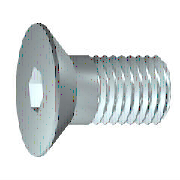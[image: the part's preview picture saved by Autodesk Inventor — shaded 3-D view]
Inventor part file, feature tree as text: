
AUTODESK INVENTOR PART (.ipt)
format: ipt  version: 2020 (Build 240168000, 168)  size: 186,368 bytes
history: native  units: mm (DEFAULTED — no unit token found)
features: other x4, sketch x3, fillet x1, chamfer x1
ambient origin geometry x8: Origin, YZ Plane, XZ Plane, XY Plane, X Axis, Y Axis, Z Axis, Center Point
bodies: Solid1 (feature_tree)
feature tree (9):
  sketch  "Sketch1"  dims[d2=3.0mm]
  other  "WorkPoint1"
  sketch  "Sketch2"  dims[d3=3.0mm]
  fillet  "Fillet1"  [1 undecoded]
  chamfer  "Chamfer1"  Distance=1.5mm
  other  "MSC_A1"
  other  "MSC_PF1"
  other  "MSC_PT1"
  sketch  "Sketch3"  dims[d4=1.5mm d5=1.5mm d6=8.0mm d7=25.0mm d8=360.0deg d9=0.0mm d10=2.0mm d11=2.0mm d12=120.0deg d13=120.0deg d14=120.0deg d15=120.0deg d16=1.2mm d17=0.0mm d18=0.1mm d19=0.25mm d20=45.0deg d22=0.0mm d23=0.0mm d35=0.0mm d37=0.0mm d38=0.0mm d39=0.25mm d40=0.0mm d41=0.0mm d42=0.0mm d43=45.0deg]
note: 1 required parameter value undecoded (feature->parameter linkage not recoverable at this tier; creation-order binding heuristic only, values carry confidence <= 0.55)
